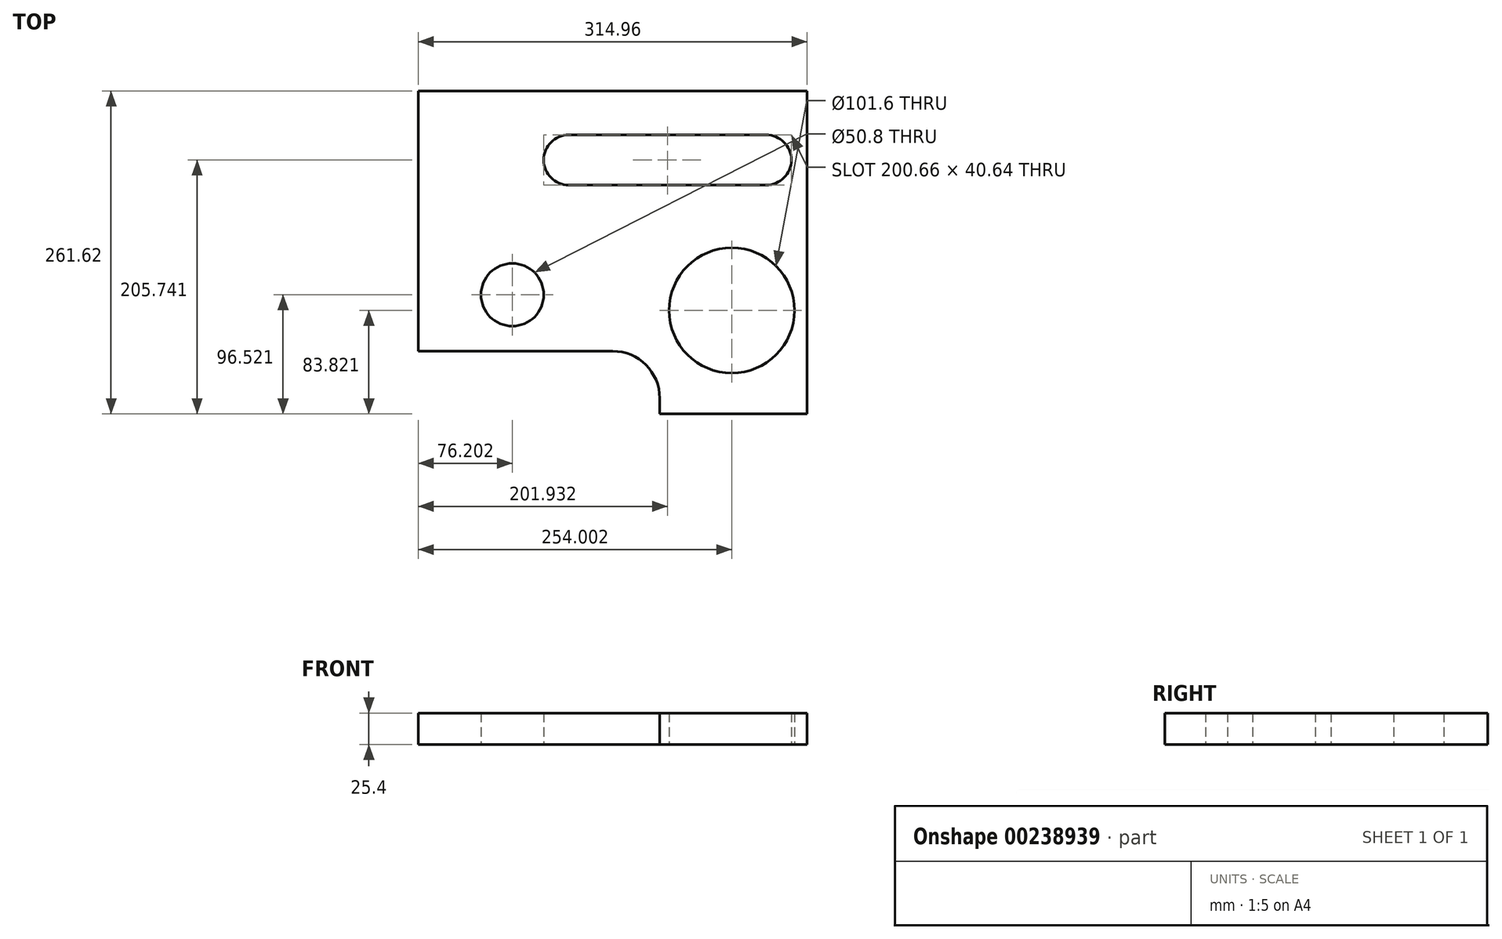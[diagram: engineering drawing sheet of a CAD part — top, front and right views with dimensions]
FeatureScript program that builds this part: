
annotation { "Feature Type Name" : "Feature", "Feature Type Description" : "" }
export const myFeature = defineFeature(function(context is Context, id is Id, definition is map)
    precondition{}
    {
        {
            var Q0;
            Q0=qCreatedBy(makeId("Top.planeOp"),FACE);
            var sketch = newSketch(context, id + "F0", { "sketchPlane" : qUnion([Q0])});
            skLineSegment(sketch, "E0", {"start": v(-136.25, 106.9) * mm, "end": v(178.71, 106.9) * mm});
            skLineSegment(sketch, "E1", {"start": v(178.71, 106.9) * mm, "end": v(178.71, -154.72) * mm});
            skLineSegment(sketch, "E2", {"start": v(178.71, -154.72) * mm, "end": v(59.33, -154.72) * mm});
            skLineSegment(sketch, "E3", {"start": v(59.33, -154.72) * mm, "end": v(59.33, -142.02) * mm});
            skLineSegment(sketch, "E4", {"start": v(-136.25, 106.9) * mm, "end": v(-136.25, -103.92) * mm});
            skLineSegment(sketch, "E5", {"start": v(-136.25, -103.92) * mm, "end": v(21.23, -103.92) * mm});
            skPoint(sketch, "E6.visualSharp", {"position": v(59.33, -103.92) * mm});
            skArc(sketch, "E6.filletArc", {"start": v(59.33, -142.02) * mm, "mid": v(48.17, -115.08) * mm, "end": v(21.23, -103.92) * mm});
            skLineSegment(sketch, "E7", {"start": v(178.71, -154.72) * mm, "end": v(117.75, -154.72) * mm});
            skLineSegment(sketch, "E8", {"start": v(117.75, -154.72) * mm, "end": v(117.75, -70.9) * mm});
            skCircle(sketch, "E9", {"center": v(117.75, -70.9) * mm, "radius": 50.8 * mm});
            skLineSegment(sketch, "E10", {"start": v(-136.25, -103.92) * mm, "end": v(-136.25, -58.2) * mm});
            skLineSegment(sketch, "E11", {"start": v(-136.25, -58.2) * mm, "end": v(-60.05, -58.2) * mm});
            skCircle(sketch, "E12", {"center": v(-60.05, -58.2) * mm, "radius": 25.4 * mm});
            skLineSegment(sketch, "E13", {"start": v(178.71, 106.9) * mm, "end": v(178.71, 30.7) * mm});
            skLineSegment(sketch, "E14", {"start": v(166.01, 51.02) * mm, "end": v(166.01, 51.02) * mm});
            skLineSegment(sketch, "E15", {"start": v(145.7, 71.34) * mm, "end": v(-14.33, 71.34) * mm});
            skLineSegment(sketch, "E16", {"start": v(-34.65, 51.02) * mm, "end": v(-34.65, 51.02) * mm});
            skLineSegment(sketch, "E17", {"start": v(-14.33, 30.7) * mm, "end": v(145.7, 30.7) * mm});
            skPoint(sketch, "E18.visualSharp", {"position": v(-34.65, 71.34) * mm});
            skArc(sketch, "E18.filletArc", {"start": v(-14.33, 71.34) * mm, "mid": v(-28.7, 65.39) * mm, "end": v(-34.65, 51.02) * mm});
            skPoint(sketch, "E19.visualSharp", {"position": v(-34.65, 30.7) * mm});
            skArc(sketch, "E19.filletArc", {"start": v(-34.65, 51.02) * mm, "mid": v(-28.7, 36.65) * mm, "end": v(-14.33, 30.7) * mm});
            skPoint(sketch, "E20.visualSharp", {"position": v(166.01, 30.7) * mm});
            skArc(sketch, "E20.filletArc", {"start": v(145.7, 30.7) * mm, "mid": v(160.06, 36.65) * mm, "end": v(166.01, 51.02) * mm});
            skPoint(sketch, "E21.visualSharp", {"position": v(166.01, 71.34) * mm});
            skArc(sketch, "E21.filletArc", {"start": v(166.01, 51.02) * mm, "mid": v(160.06, 65.39) * mm, "end": v(145.7, 71.34) * mm});
            skSolve(sketch);
        }
        {
            var Q0;
            Q0 = qSketchRegion(id + "F0", true);
            extrude(context, id + "F1", {"entities" : qUnion([Q0]), "depth" : 25.4 * mm});
        }
    });
